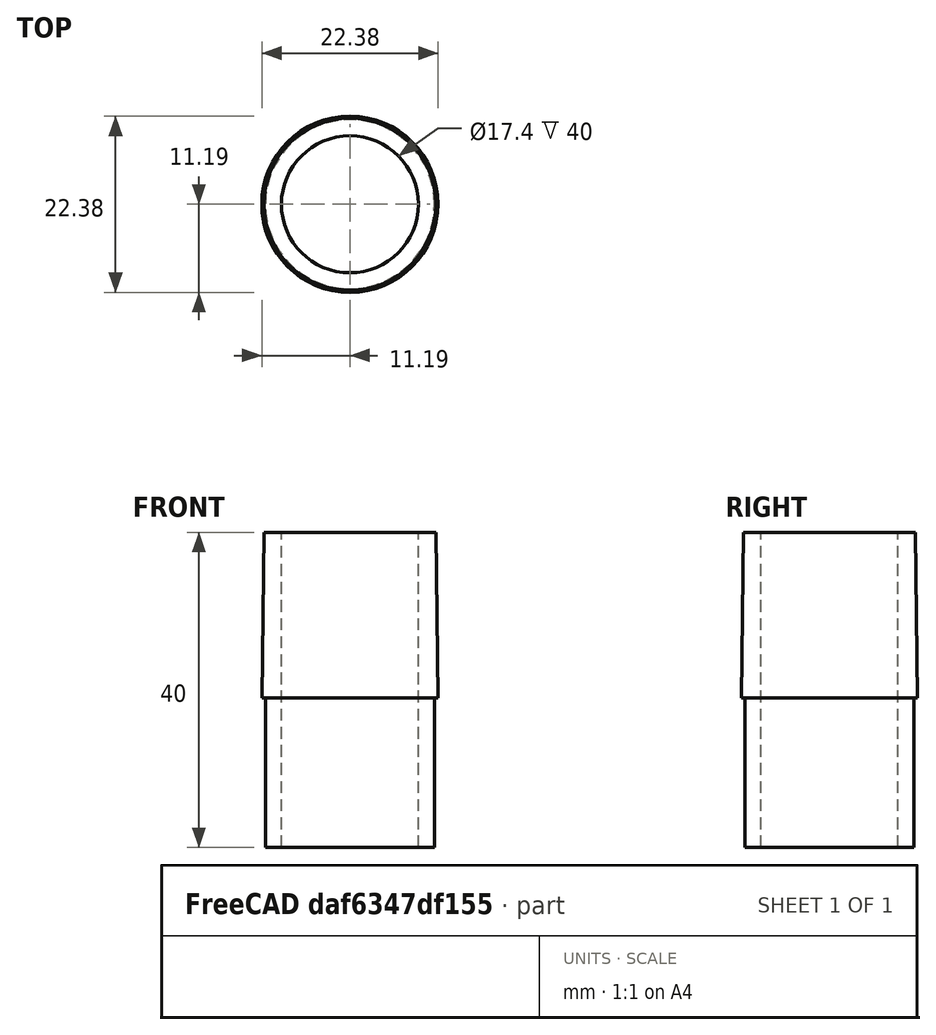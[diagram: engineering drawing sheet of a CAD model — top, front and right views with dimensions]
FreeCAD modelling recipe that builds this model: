
FCSTD DOCUMENT  (FreeCAD 0.18R4 (GitTag))
Label: BlowerOutletAdapter-V3
License: All rights reserved
LicenseURL: http://en.wikipedia.org/wiki/All_rights_reserved
objects: Part::Cylinder×2, Part::Cone×1, Part::MultiFuse×1, Part::Cut×1
note: 5 computed .brp shape members not serialized (recipe doc carries the construction recipe); baked Part::Feature solids carry a one-line shape summary decoded from their .brp

FEATURE [Part::Cone] Cone001  label="22mmTaper"
  Angle = 360
  AttacherType = Attacher::AttachEngine3D
  Height = 21
  Placement = pos=(0,0,19) rot=(0,0,1;0rad)
  Radius1 = 11.19
  Radius2 = 10.92
FEATURE [Part::Cylinder] Cylinder005  label="OutletExtension"
  Angle = 360
  AttacherType = Attacher::AttachEngine3D
  Height = 40
  Radius = 8.7
FEATURE [Part::Cylinder] Cylinder007  label="HousingOutlet"
  Angle = 360
  AttacherType = Attacher::AttachEngine3D
  Height = 40
  Radius = 10.75
FEATURE [Part::MultiFuse] Fusion  label="Outside"
  Shapes = -> [Cone001,Cylinder007]
FEATURE [Part::Cut] Cut  label="BlowerOutletAdapter-V3"
  Base = -> Fusion
  Tool = -> Cylinder005
